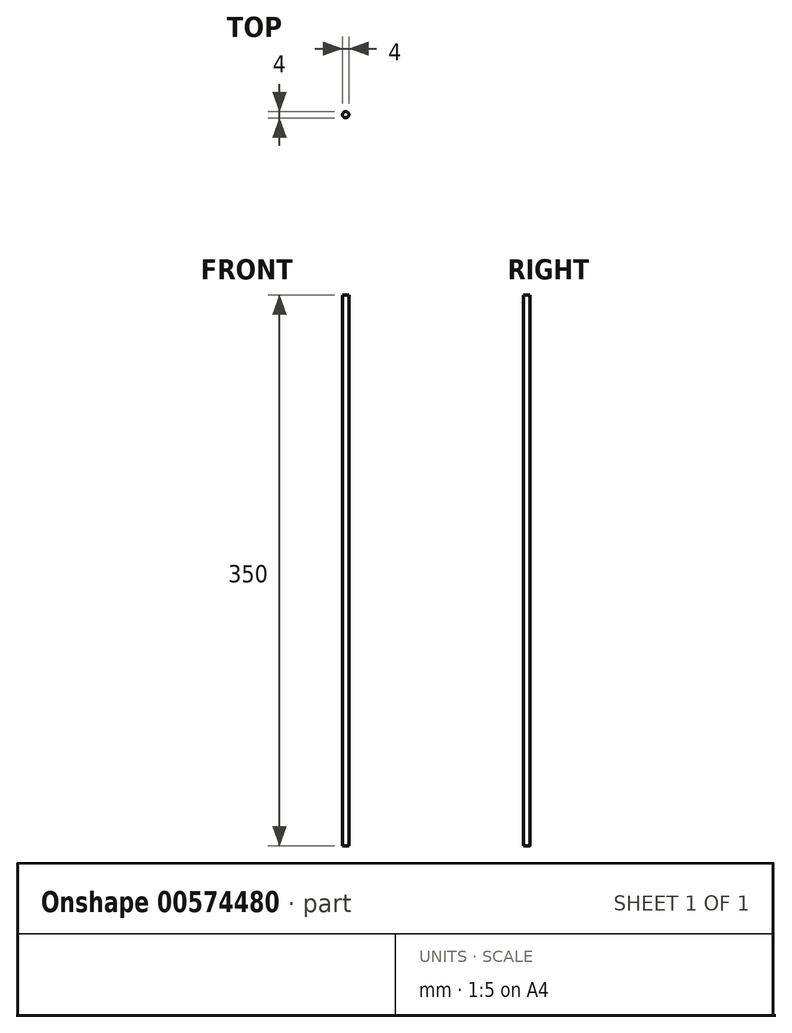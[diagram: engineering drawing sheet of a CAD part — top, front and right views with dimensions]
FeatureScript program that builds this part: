
annotation { "Feature Type Name" : "Feature", "Feature Type Description" : "" }
export const myFeature = defineFeature(function(context is Context, id is Id, definition is map)
    precondition{}
    {
        {
            var Q0;
            Q0=qCreatedBy(makeId("Top.planeOp"),FACE);
            var sketch = newSketch(context, id + "F0", { "sketchPlane" : qUnion([Q0])});
            skCircle(sketch, "E0", {"center": v(0, 0) * mm, "radius": 2 * mm});
            skSolve(sketch);
        }
        {
            var Q0;
            Q0=makeQuery(id+"F0.imprint","IMPRINT",FACE,{"disambiguationData":[TD([[makeQuery(id+"F0.imprint","IMPRINT",EDGE,{"derivedFrom":sQuery(id+"F0.wireOp",EDGE,"E0")}),1.0]])]});
            extrude(context, id + "F1", {"entities" : qUnion([Q0]), "depth" : 350 * mm, "offsetDistance" : 25 * mm});
        }
    });
